annotation { "Feature Type Name" : "Feature", "Feature Type Description" : "" }
export const myFeature = defineFeature(function(context is Context, id is Id, definition is map)
    precondition{}
    {
        {
            var Q0;
            Q0=qCreatedBy(makeId("Top.planeOp"),FACE);
            var sketch = newSketch(context, id + "F0", { "sketchPlane" : qUnion([Q0])});
            skLineSegment(sketch, "E0.bottom", {"start": v(3.05, 0) * mm, "end": v(91.95, 0) * mm});
            skLineSegment(sketch, "E0.top", {"start": v(3.05, 56.9) * mm, "end": v(91.95, 56.9) * mm});
            skLineSegment(sketch, "E0.left", {"start": v(0, 3.05) * mm, "end": v(0, 53.85) * mm});
            skLineSegment(sketch, "E0.right", {"start": v(95, 3.05) * mm, "end": v(95, 53.85) * mm});
            skCircle(sketch, "E1", {"center": v(3.05, 3.05) * mm, "radius": 1.52 * mm});
            skCircle(sketch, "E2.0.1.0", {"center": v(3.05, 53.85) * mm, "radius": 1.52 * mm});
            skCircle(sketch, "E2.1.0.0", {"center": v(91.95, 3.05) * mm, "radius": 1.52 * mm});
            skCircle(sketch, "E2.1.1.0", {"center": v(91.95, 53.85) * mm, "radius": 1.52 * mm});
            skLineSegment(sketch, "E2.direction1", {"start": v(3.05, 3.05) * mm, "end": v(91.95, 3.05) * mm, "construction": true});
            skLineSegment(sketch, "E2.direction2", {"start": v(3.05, 3.05) * mm, "end": v(3.05, 53.85) * mm, "construction": true});
            skPoint(sketch, "E3.visualSharp", {"position": v(0, 56.9) * mm});
            skArc(sketch, "E3.filletArc", {"start": v(3.05, 56.9) * mm, "mid": v(0.9, 56) * mm, "end": v(0, 53.85) * mm});
            skPoint(sketch, "E4.visualSharp", {"position": v(95, 56.9) * mm});
            skArc(sketch, "E4.filletArc", {"start": v(95, 53.85) * mm, "mid": v(94.1, 56) * mm, "end": v(91.95, 56.9) * mm});
            skPoint(sketch, "E5.visualSharp", {"position": v(95, 0) * mm});
            skArc(sketch, "E5.filletArc", {"start": v(91.95, 0) * mm, "mid": v(94.1, 0.9) * mm, "end": v(95, 3.05) * mm});
            skPoint(sketch, "E6.visualSharp", {"position": v(0, 0) * mm});
            skArc(sketch, "E6.filletArc", {"start": v(0, 3.05) * mm, "mid": v(0.9, 0.9) * mm, "end": v(3.05, 0) * mm});
            skCircle(sketch, "E7", {"center": v(20.45, 4.32) * mm, "radius": 1.2 * mm});
            skCircle(sketch, "E8", {"center": v(20.45, 52.58) * mm, "radius": 1.2 * mm});
            skCircle(sketch, "E9", {"center": v(86.49, 7.5) * mm, "radius": 1.2 * mm});
            skCircle(sketch, "E10", {"center": v(86.49, 49.4) * mm, "radius": 1.2 * mm});
            skSolve(sketch);
        }
        {
            var Q0;
            Q0=qSketchRegion(id+"F0",true);
            extrude(context, id + "F1", {"entities" : qUnion([Q0]), "depth" : 3 * mm});
        }
        {
            var Q0;
            Q0=makeQuery(id+"F1.opExtrude","CAP_FACE",FACE,{"disambiguationData":[OSD([sQuery(id+"F0.wireOp",EDGE,"E0.bottom"),sQuery(id+"F0.wireOp",EDGE,"E0.top"),sQuery(id+"F0.wireOp",EDGE,"E0.left"),sQuery(id+"F0.wireOp",EDGE,"E0.right"),sQuery(id+"F0.wireOp",EDGE,"E1"),sQuery(id+"F0.wireOp",EDGE,"E2.0.1.0"),sQuery(id+"F0.wireOp",EDGE,"E2.1.0.0"),sQuery(id+"F0.wireOp",EDGE,"E2.1.1.0"),sQuery(id+"F0.wireOp",EDGE,"pod769ia-tjEz-awd3-bj1G-7ihdWW67tKTp"),sQuery(id+"F0.wireOp",EDGE,"xes5iXTk-P3TU-gzOc-iE2A-xvNo2476WRCw"),sQuery(id+"F0.wireOp",EDGE,"99gb05hv-srND-eTdO-F1NF-LBFHHsY0706o"),sQuery(id+"F0.wireOp",EDGE,"Ib4fIEhX-f6eD-Fh0k-qnpB-C0oVsota3eAH"),sQuery(id+"F0.wireOp",EDGE,"E3.filletArc"),sQuery(id+"F0.wireOp",EDGE,"E4.filletArc"),sQuery(id+"F0.wireOp",EDGE,"E5.filletArc"),sQuery(id+"F0.wireOp",EDGE,"E6.filletArc")])],"isStart":false});
            var sketch = newSketch(context, id + "F2", { "sketchPlane" : qUnion([Q0])});
            skText(sketch, "E11", { "text": "77330-131", "fontName": "OpenSans-Regular.ttf"});
            skText(sketch, "E12", { "text": "BEAGLEBONE BLACK ADAPTER PLATE", "fontName": "OpenSans-Regular.ttf"});
            skText(sketch, "E13", { "text": "MAXIMUM MODULARITY", "fontName": "OpenSans-Regular.ttf"});
            const initialGuessF2  = {"E11": [0.00127, 0.0397, 0, -1, 0.00386], "E12": [0.00952, 0.0254, 1, 0, 0.00315], "E13": [0.09436, 0.00686, 0, 1, 0.0027]};
            skSetInitialGuess(sketch, initialGuessF2);
            skSolve(sketch);
        }
        {
            var Q0;
            Q0=qSketchRegion(id+"F2",true);
            extrude(context, id + "F3", {"entities" : qUnion([Q0]), "operationType" : NewBodyOperationType.REMOVE, "oppositeDirection" : true, "depth" : 0.25 * mm});
        }
    });